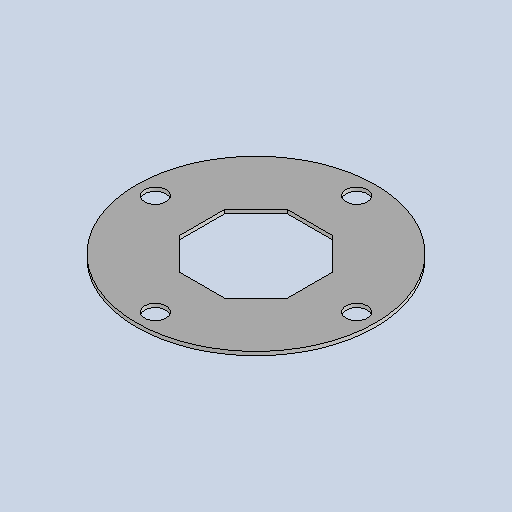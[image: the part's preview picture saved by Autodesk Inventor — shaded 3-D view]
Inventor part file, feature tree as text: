
AUTODESK INVENTOR PART (.ipt)
format: ipt  version: 2025.1 (Build 291241020, 241B)  size: 175,616 bytes
history: native  units: mm
features: other x4, sketch x2, sheet_metal_op x1, pattern_circular x1
ambient origin geometry x8: Origin, YZ Plane, XZ Plane, XY Plane, X Axis, Y Axis, Z Axis, Center Point
bodies: Body1 (feature_tree)
feature tree (8):
  sheet_metal_op  "Face3"
  pattern_circular  "Circular Pattern1"  Count=50  [1 undecoded]
  other  "Corner Chamfer2"
  sketch  "Sketch1"  dims[d156=3.0mm]
  other  "Plate5"
  sketch  "Sketch7"  dims[d157=190.0mm d158=86.0mm d159=86.0mm d160=17.0mm d161=80.0mm d162=3.0mm d163=0.0mm d164=40.0mm d165=360.0deg d167=25.0mm d168=6.0mm d169=45.0deg]
  other  "Cut1"
  other  "Definition1"
note: 1 required parameter value undecoded (feature->parameter linkage not recoverable at this tier; creation-order binding heuristic only, values carry confidence <= 0.55)
